# Revit family: Inland_2-seater_sofa_leather_AV22
name_source: partatom
category: Furniture
revit_build: Autodesk Revit 2017 (Build: 20171027_0315(x64)
units: mm (PartAtom-declared; Revit-internal decimal feet)

## family parameters
Always vertical = Yes
Cut with Voids When Loaded = No
OmniClass Number = 23.40.20.00
OmniClass Title = General Furniture and Specialties
Room Calculation Point = No
Shared = No
Work Plane-Based = No

## types (1)
- Inland_2-seater_sofa_leather_AV22
    Base = &tradition Powder Coated Metal black matt
    Depth = 92cm/36,2in
    Description = A square, high-armed sofa with a black steel-footed base, Anderssen & Voll’s Inland showcases an Italian approach to a classic mid-century modern lounge piece. Featuring the plush cushion seating of typical Italian designs, Inland comes available as either a two-seater or a three-seater in a number of upholstery options.
    Design = Anderssen & Voll
    Design Year = 2022
    Height = 68cm/26,8in
    Manufacturer = &Tradition
    Model = Inland 2-seater sofa AV22
    Packaging dimensions & weight = Please see product fact sheet available from download page on website
    Seat Height = 38,5cm/15,2in
    Type Comments = Inland
    URL = https://www.andtradition.com
    Upholstery = &tradition Camo Silk Black
    Variation = Please visit our website to see available colours and finishes.
    Width = 176cm/69,3in

## geometry (parser evidence)
native form markers: Sweep x2
no freeform markers — native parametric forms only
